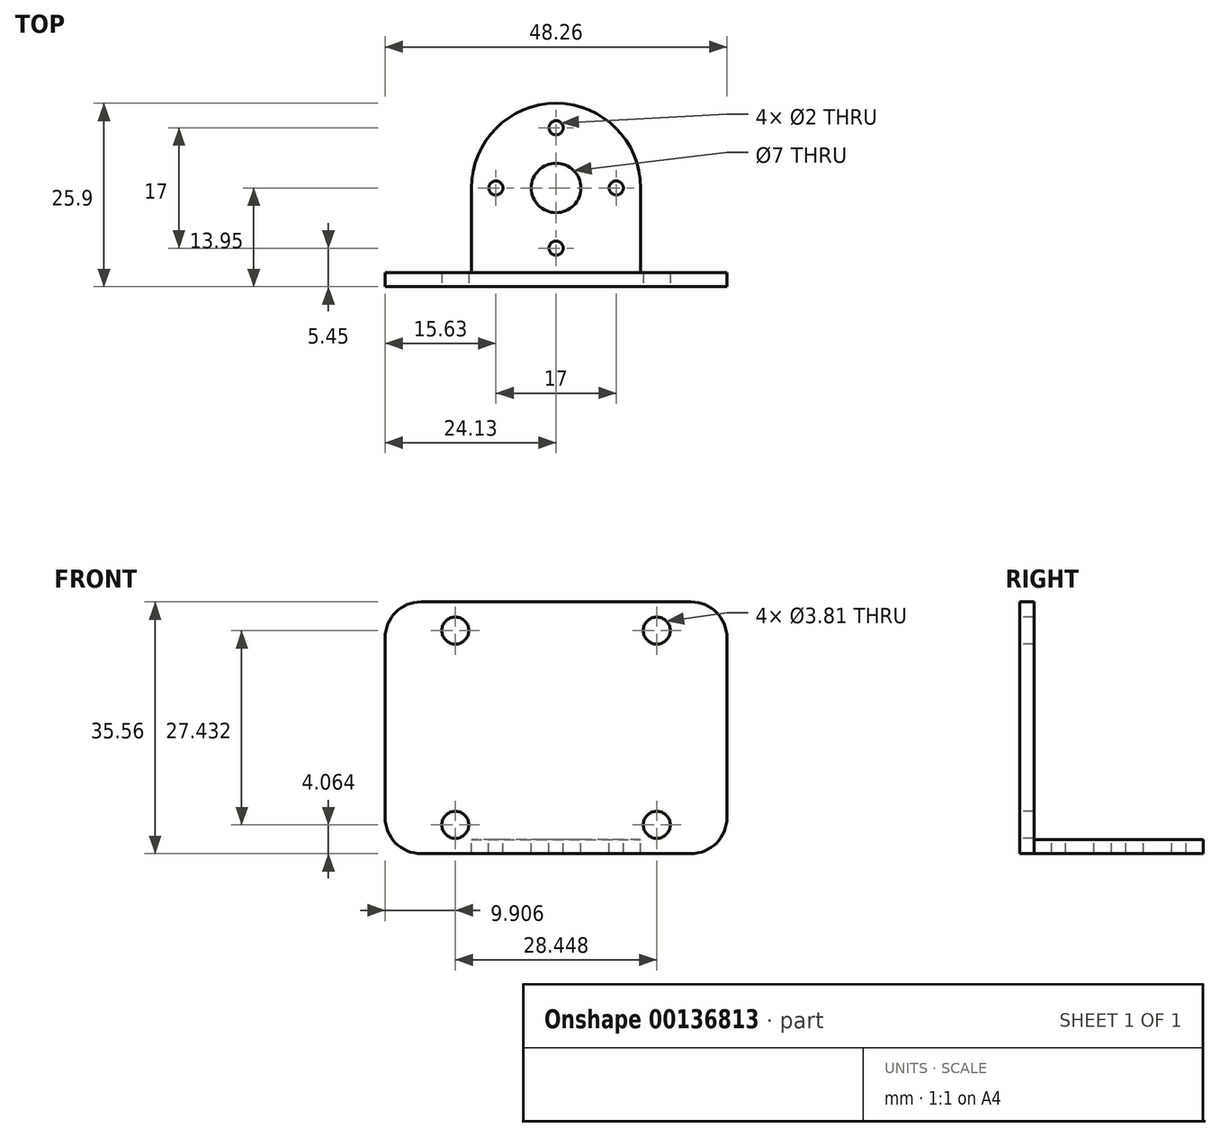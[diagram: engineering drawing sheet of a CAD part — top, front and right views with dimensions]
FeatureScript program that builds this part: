
annotation { "Feature Type Name" : "Feature", "Feature Type Description" : "" }
export const myFeature = defineFeature(function(context is Context, id is Id, definition is map)
    precondition{}
    {
        {
            var Q0;
            Q0=qCreatedBy(makeId("Top.planeOp"),FACE);
            var sketch = newSketch(context, id + "F0", { "sketchPlane" : qUnion([Q0])});
            skCircle(sketch, "E0", {"center": v(0, 0) * mm, "radius": 11.95 * mm});
            skLineSegment(sketch, "E1.bottom", {"start": v(24.13, -11.95) * mm, "end": v(-24.13, -11.95) * mm});
            skLineSegment(sketch, "E1.top", {"start": v(24.13, -13.95) * mm, "end": v(-24.13, -13.95) * mm});
            skLineSegment(sketch, "E1.left", {"start": v(24.13, -11.95) * mm, "end": v(24.13, -13.95) * mm});
            skLineSegment(sketch, "E1.right", {"start": v(-24.13, -11.95) * mm, "end": v(-24.13, -13.95) * mm});
            skPoint(sketch, "E1.middle", {"position": v(0, -12.95) * mm});
            skLineSegment(sketch, "E2", {"start": v(11.95, 0) * mm, "end": v(11.95, -11.95) * mm});
            skLineSegment(sketch, "E3", {"start": v(-11.95, 0) * mm, "end": v(-11.95, -11.95) * mm});
            skCircle(sketch, "E4", {"center": v(0, 0) * mm, "radius": 3.5 * mm});
            skLineSegment(sketch, "E5", {"start": v(0, 0) * mm, "end": v(-8.5, 0) * mm});
            skLineSegment(sketch, "E6", {"start": v(0, 0) * mm, "end": v(0, 8.5) * mm});
            skLineSegment(sketch, "E7.MirrorCS", {"start": v(0, 0) * mm, "end": v(0, -8.5) * mm});
            skLineSegment(sketch, "E8.MirrorCS", {"start": v(0, 0) * mm, "end": v(8.5, 0) * mm});
            skSolve(sketch);
        }
        {
            var Q0;
            Q0 = qSketchRegion(id + "F0", true);
            extrude(context, id + "F1", {"entities" : qUnion([Q0]), "oppositeDirection" : true, "depth" : 2 * mm});
        }
        {
            var Q0;
            Q0=makeQuery(id+"F1.opExtrude","CAP_FACE",FACE,{"disambiguationData":[OSD([sQuery(id+"F0.wireOp",EDGE,"E0"),sQuery(id+"F0.wireOp",EDGE,"E1.bottom"),sQuery(id+"F0.wireOp",EDGE,"E1.top"),sQuery(id+"F0.wireOp",EDGE,"E1.left"),sQuery(id+"F0.wireOp",EDGE,"E1.right"),sQuery(id+"F0.wireOp",EDGE,"E2"),sQuery(id+"F0.wireOp",EDGE,"E3")])],"isStart":true});
            var sketch = newSketch(context, id + "F2", { "sketchPlane" : qUnion([Q0])});
            skLineSegment(sketch, "E9.bottom", {"start": v(-24.13, -11.95) * mm, "end": v(24.13, -11.95) * mm});
            skLineSegment(sketch, "E9.top", {"start": v(-24.13, -13.95) * mm, "end": v(24.13, -13.95) * mm});
            skLineSegment(sketch, "E9.left", {"start": v(-24.13, -11.95) * mm, "end": v(-24.13, -13.95) * mm});
            skLineSegment(sketch, "E9.right", {"start": v(24.13, -11.95) * mm, "end": v(24.13, -13.95) * mm});
            skSolve(sketch);
        }
        {
            var Q0;
            Q0 = qSketchRegion(id + "F2", true);
            extrude(context, id + "F3", {"entities" : qUnion([Q0]), "operationType" : NewBodyOperationType.ADD, "depth" : 35.56 * mm - 2 * mm});
        }
        {
            var Q0;
            Q0=makeQuery(id+"F3.boolean.opBoolean","MERGE",FACE,{"derivedFrom":[makeQuery(id+"F1.opExtrude","SWEPT_FACE",FACE,{"disambiguationData":[OSD([sQuery(id+"F0.wireOp",EDGE,"E1.top")])]}),makeQuery(id+"F3.opExtrude","SWEPT_FACE",FACE,{"disambiguationData":[OSD([sQuery(id+"F2.wireOp",EDGE,"E9.top")])]})]});
            var sketch = newSketch(context, id + "F4", { "sketchPlane" : qUnion([Q0])});
            skLineSegment(sketch, "E10", {"start": v(-24.13, 15.78) * mm, "end": v(24.13, 15.78) * mm});
            skLineSegment(sketch, "E11", {"start": v(0, 15.78) * mm, "end": v(0, 33.56) * mm});
            skLineSegment(sketch, "E12.bottom", {"start": v(14.22, 29.5) * mm, "end": v(-14.22, 29.5) * mm});
            skLineSegment(sketch, "E12.top", {"start": v(14.22, 2.06) * mm, "end": v(-14.22, 2.06) * mm});
            skLineSegment(sketch, "E12.left", {"start": v(14.22, 29.5) * mm, "end": v(14.22, 2.06) * mm});
            skLineSegment(sketch, "E12.right", {"start": v(-14.22, 29.5) * mm, "end": v(-14.22, 2.06) * mm});
            skPoint(sketch, "E12.middle", {"position": v(0, 15.78) * mm});
            skSolve(sketch);
        }
        {
            var Q0;
            Q0=sQuery(id+"F4.wireOp",VERTEX,"E12.bottom.end");
            var Q1;
            Q1=sQuery(id+"F4.wireOp",VERTEX,"E12.bottom.start");
            var Q2;
            Q2=sQuery(id+"F4.wireOp",VERTEX,"E12.top.start");
            var Q3;
            Q3=sQuery(id+"F4.wireOp",VERTEX,"E12.right.end");
            var Q4;
            Q4=makeQuery(id+"F1.opExtrude","SWEPT_BODY",BODY,{"disambiguationData":[OSD([sQuery(id+"F0.wireOp",EDGE,"E0"),sQuery(id+"F0.wireOp",EDGE,"E1.bottom"),sQuery(id+"F0.wireOp",EDGE,"E1.top"),sQuery(id+"F0.wireOp",EDGE,"E1.left"),sQuery(id+"F0.wireOp",EDGE,"E1.right"),sQuery(id+"F0.wireOp",EDGE,"E2"),sQuery(id+"F0.wireOp",EDGE,"E3")])]});
            hole(context, id + "F5", {"style" : HoleStyle.SIMPLE, "endStyle" : HoleEndStyle.THROUGH, "holeDiameter" : 3.8 * mm, "locations" : qUnion([Q0, Q1, Q2, Q3]), "scope" : qUnion([Q4]), "isTappedThrough" : true});
        }
        {
            var Q0;
            Q0=makeQuery(id+"F3.opExtrude","CAP_EDGE",EDGE,{"disambiguationData":[OSD([sQuery(id+"F2.wireOp",EDGE,"E9.right")])],"isStart":false});
            var Q1;
            Q1=makeQuery(id+"F3.opExtrude","CAP_EDGE",EDGE,{"disambiguationData":[OSD([sQuery(id+"F2.wireOp",EDGE,"E9.left")])],"isStart":false});
            var Q2;
            Q2=makeQuery(id+"F1.opExtrude","CAP_EDGE",EDGE,{"disambiguationData":[OSD([sQuery(id+"F0.wireOp",EDGE,"E1.right")])],"isStart":false});
            var Q3;
            Q3=makeQuery(id+"F1.opExtrude","CAP_EDGE",EDGE,{"disambiguationData":[OSD([sQuery(id+"F0.wireOp",EDGE,"E1.left")])],"isStart":false});
            fillet(context, id + "F6", {"entities" : qUnion([Q0, Q1, Q2, Q3]), "radius" : 5.08 * mm, "tangentPropagation" : true, "allowEdgeOverflow" : false});
        }
        {
            var Q0;
            Q0=sQuery(id+"F0.wireOp",VERTEX,"E7.MirrorCS.end");
            var Q1;
            Q1=sQuery(id+"F0.wireOp",VERTEX,"E8.MirrorCS.end");
            var Q2;
            Q2=sQuery(id+"F0.wireOp",VERTEX,"E5.end");
            var Q3;
            Q3=sQuery(id+"F0.wireOp",VERTEX,"E6.end");
            var Q4;
            Q4=makeQuery(id+"F1.opExtrude","SWEPT_BODY",BODY,{"disambiguationData":[OSD([sQuery(id+"F0.wireOp",EDGE,"E0"),sQuery(id+"F0.wireOp",EDGE,"E1.bottom"),sQuery(id+"F0.wireOp",EDGE,"E1.top"),sQuery(id+"F0.wireOp",EDGE,"E1.left"),sQuery(id+"F0.wireOp",EDGE,"E1.right"),sQuery(id+"F0.wireOp",EDGE,"E2"),sQuery(id+"F0.wireOp",EDGE,"E3"),sQuery(id+"F0.wireOp",EDGE,"E4")])]});
            hole(context, id + "F7", {"style" : HoleStyle.SIMPLE, "endStyle" : HoleEndStyle.THROUGH, "holeDiameter" : 2 * mm, "locations" : qUnion([Q0, Q1, Q2, Q3]), "scope" : qUnion([Q4]), "isTappedThrough" : true});
        }
    });
